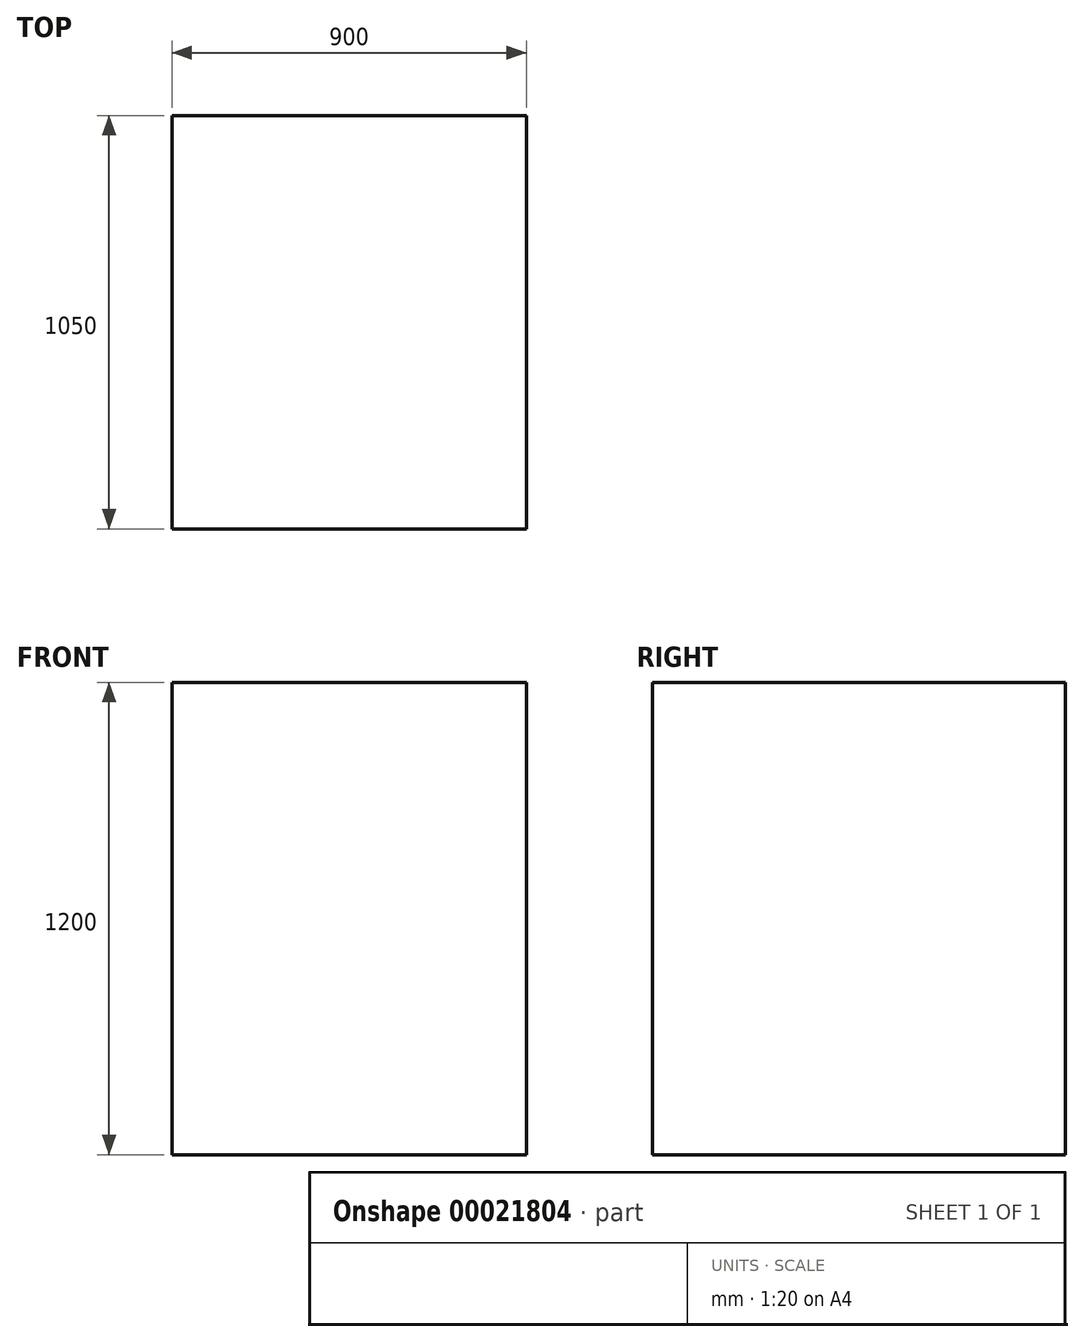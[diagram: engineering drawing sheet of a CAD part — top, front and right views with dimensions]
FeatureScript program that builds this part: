
annotation { "Feature Type Name" : "Feature", "Feature Type Description" : "" }
export const myFeature = defineFeature(function(context is Context, id is Id, definition is map)
    precondition{}
    {
        {
            var Q0;
            Q0=qCreatedBy(makeId("Top.planeOp"),FACE);
            var sketch = newSketch(context, id + "F0", { "sketchPlane" : qUnion([Q0])});
            skLineSegment(sketch, "E0.bottom", {"start": v(0, 0) * mm, "end": v(900, 0) * mm});
            skLineSegment(sketch, "E0.top", {"start": v(0, 1050) * mm, "end": v(900, 1050) * mm});
            skLineSegment(sketch, "E0.left", {"start": v(0, 0) * mm, "end": v(0, 1050) * mm});
            skLineSegment(sketch, "E0.right", {"start": v(900, 0) * mm, "end": v(900, 1050) * mm});
            skSolve(sketch);
        }
        {
            var Q0;
            Q0=makeQuery(id+"F0.imprint","IMPRINT",FACE,{"disambiguationData":[TD([[makeQuery(id+"F0.imprint","IMPRINT",EDGE,{"derivedFrom":sQuery(id+"F0.wireOp",EDGE,"E0.bottom")}),1.0]])]});
            extrude(context, id + "F1", {"entities" : qUnion([Q0]), "depth" : 1200 * mm});
        }
    });
